# Revit family: Deca_Bacia para caixa acoplada_Aspen_P.750
name_source: partatom
category: Plumbing Fixtures
units: mm (PartAtom-declared; Revit-internal decimal feet)

## family parameters
Cut with Voids When Loaded = No
Host = Face
Part Type = Normal
Room Calculation Point = No
Round Connector Dimension = Use Radius
Shared = No

## types (8) — shared parameters
Acompanha o Produto = -
Aprovado por = quattroD
Atendimento ao Cliente = 0800-0117073
Categoria = BACIAS E BIDES
Composição Anel Vedação = Não Possui
Composição Assento = -
Composição Básica = Argila, feldspato, caulim, vidrados e corantes inorgânicos.
Composição Componente = Não Possui
Consumo = 6 lpf
Cor Interna = -
Cor Secundária = -
Cores Componente = -
Criado por = quattroD
Código Pai = P.750
Description = Bacia para caixa acoplada
Diâmetro Ponto de Esgoto = 100 mm  [stored 0.328084 ft]
Diâmetro Água Fria = 15 mm  [stored 0.0492126 ft]
Informações Complementares = -
Itens de Instalação = -
Linha = Aspen
Manufacturer = Deca
Norma = NBR-16727-1;NBR-16727-2
Pressão máx. funcionamento = -
Pressão mín. Aquec. Acúmulo = -
Pressão mín. Aquec. Passagem = -
Pressão mín. funcionamento = -
Raio Ponto de Esgoto = 50 mm  [stored 0.164042 ft]
Raio Água Fria = 8 mm  [stored 0.0262467 ft]
Saída de Esgoto = Saída de Esgoto Vertical
Segmento = Banheiro Competitivo
Tipo de dispositivo economizador = -
Tipo de mecanismo utilizado = -
Tipo de rosca de entrada = -
Tipo de rosca de saída = -
URL = www.deca.com.br
Vazão na Pressão máx. (L/min) = -
Vazão na Pressão mín. (L/min) = -
zero-valued in all types: CWFU, Default Elevation, WFU

## per-type parameters (varying)
| type | Combinação | Cor Principal | Material | Model | Peso Líquido (Kg) |
| P.750.37_Creme_CD.00F.37 | Deca_Caixa acoplada com acionamento Duo_Aspen-Izy-Ravena-Fast-Flex_CD.00F : CD.00F.37_Creme | Creme | Deca_Creme | P.750.37 | 16 |
| P.750.17_Branco_CD.00F.17 | Deca_Caixa acoplada com acionamento Duo_Aspen-Izy-Ravena-Fast-Flex_CD.00F : CD.00F.17_Branco | Branco | Deca_Branco | P.750.17 | 17 |
| P.750.95_Ébano_CD.00.95 | Deca_Caixa acoplada_Aspen-Izy-Ravena-Fast-Flex_CD.00 : CD.00.95_Ébano | Ébano | Deca_Ébano | P.750.95 | 17 |
| P.750.87_Cinza_CD.00F.87 | Deca_Caixa acoplada com acionamento Duo_Aspen-Izy-Ravena-Fast-Flex_CD.00F : CD.00F.87_Cinza | Cinza Real | Deca_Cinza | P.750.87 | 17 |
| P.750.17_Branco_CD.00.17 | Deca_Caixa acoplada_Aspen-Izy-Ravena-Fast-Flex_CD.00 : CD.00.17_Branco | Branco | Deca_Branco | P.750.17 | 17 |
| P.750.37_Creme_CD.00.37 | Deca_Caixa acoplada_Aspen-Izy-Ravena-Fast-Flex_CD.00 : CD.00.37_Creme | Creme | Deca_Creme | P.750.37 | 16 |
| P.750.87_Cinza_CD.00.87 | Deca_Caixa acoplada_Aspen-Izy-Ravena-Fast-Flex_CD.00 : CD.00.87_Cinza | Cinza Real | Deca_Cinza | P.750.87 | 17 |
| P.750.95_Ébano_CD.00F.95 | Deca_Caixa acoplada com acionamento Duo_Aspen-Izy-Ravena-Fast-Flex_CD.00F : CD.00F.95_Ébano | Ébano | Deca_Ébano | P.750.95 | 17 |

note: [stored X ft] marks values corroborated as IEEE doubles in the binary element streams (Revit-internal decimal feet)

## geometry (parser evidence)
native form markers: Sweep x8
no freeform markers — native parametric forms only
